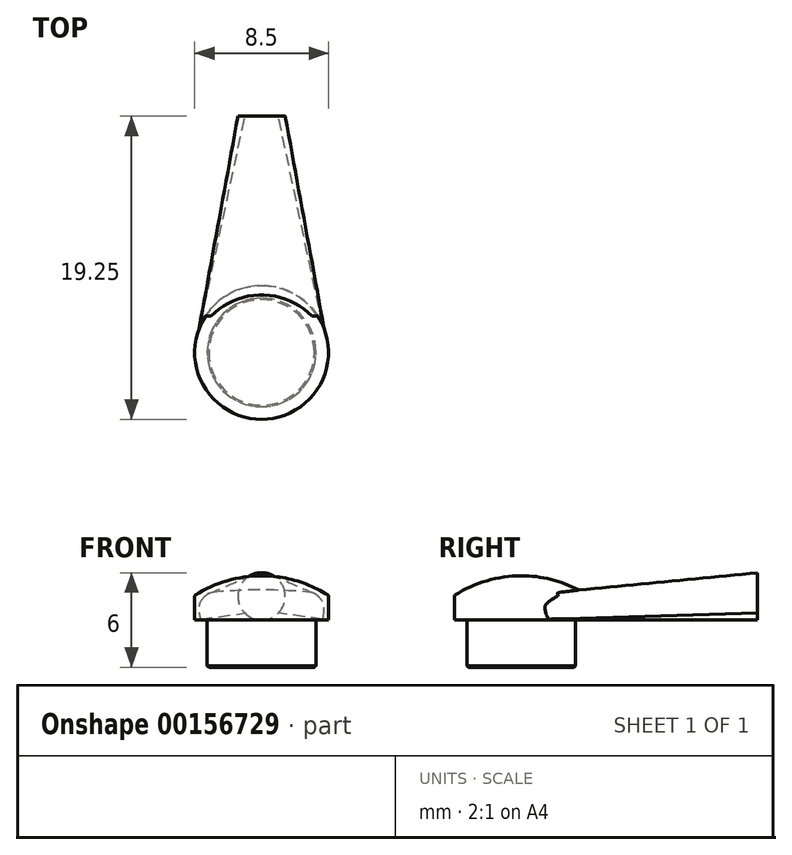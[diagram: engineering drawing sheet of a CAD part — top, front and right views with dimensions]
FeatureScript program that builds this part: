
annotation { "Feature Type Name" : "Feature", "Feature Type Description" : "" }
export const myFeature = defineFeature(function(context is Context, id is Id, definition is map)
    precondition{}
    {
        {
            var Q0;
            Q0=qCreatedBy(makeId("Top.planeOp"),FACE);
            var sketch = newSketch(context, id + "F0", { "sketchPlane" : qUnion([Q0])});
            skArc(sketch, "E0", {"start": v(-4.25, 0) * mm, "mid": v(0, -4.25) * mm, "end": v(4.25, 0) * mm});
            skArc(sketch, "E1", {"start": v(4.25, 0) * mm, "mid": v(0, 4.25) * mm, "end": v(-4.25, 0) * mm});
            skSolve(sketch);
        }
        {
            var Q0;
            Q0=makeQuery(id+"F0.imprint","IMPRINT",FACE,{"disambiguationData":[TD([[makeQuery(id+"F0.imprint","IMPRINT",EDGE,{"derivedFrom":sQuery(id+"F0.wireOp",EDGE,"E0")}),1.0]])]});
            var sketch = newSketch(context, id + "F1", { "sketchPlane" : qUnion([Q0])});
            skCircle(sketch, "E2", {"center": v(0, 0) * mm, "radius": 3.45 * mm});
            skSolve(sketch);
        }
        {
            var Q0;
            Q0=makeQuery(id+"F1.imprint","IMPRINT",FACE,{"disambiguationData":[TD([[makeQuery(id+"F1.imprint","IMPRINT",EDGE,{"derivedFrom":sQuery(id+"F1.wireOp",EDGE,"E2")}),1.0]])]});
            extrude(context, id + "F2", {"entities" : qUnion([Q0]), "oppositeDirection" : true, "depth" : 3 * mm});
        }
        {
            var Q0;
            Q0=makeQuery(id+"F2.opExtrude","CAP_EDGE",EDGE,{"disambiguationData":[OSD([sQuery(id+"F1.wireOp",EDGE,"E2")])],"isStart":false});
            chamfer(context, id + "F3", {"entities" : qUnion([Q0]), "width" : .1 * mm, "tangentPropagation" : true});
        }
        {
            var Q0;
            Q0=qCreatedBy(makeId("Front.planeOp"),FACE);
            var sketch = newSketch(context, id + "F4", { "sketchPlane" : qUnion([Q0])});
            skLineSegment(sketch, "E3.0", {"start": v(0, 0) * mm, "end": v(4.25, 0) * mm, "construction": true});
            skLineSegment(sketch, "E4.bottom", {"start": v(0, 0) * mm, "end": v(4.25, 0) * mm});
            skLineSegment(sketch, "E4.right", {"start": v(4.25, 0) * mm, "end": v(4.25, 1.55) * mm});
            skPoint(sketch, "E5.visualSharp", {"position": v(-3.75, 1.25) * mm});
            skPoint(sketch, "E6.visualSharp", {"position": v(4.25, 1.25) * mm});
            skPoint(sketch, "E7.orphan", {"position": v(-3.5, 1.25) * mm});
            skPoint(sketch, "E8.orphan", {"position": v(-4.25, 0) * mm});
            skPoint(sketch, "E9.orphan", {"position": v(3.5, 1.25) * mm});
            skPoint(sketch, "E10.end.orphan", {"position": v(0, 2.81) * mm});
            skPoint(sketch, "E11.end.orphan", {"position": v(0, 1.25) * mm});
            skArc(sketch, "E12", {"start": v(4.25, 1.55) * mm, "mid": v(2.22, 2.49) * mm, "end": v(0, 2.81) * mm});
            skLineSegment(sketch, "E13", {"start": v(0, 2.81) * mm, "end": v(0, 0) * mm});
            skSolve(sketch);
        }
        {
            var Q0;
            Q0 = qSketchRegion(id + "F4", true);
            var Q1;
            Q1=sQuery(id+"F4.wireOp",EDGE,"E13");
            revolve(context, id + "F5", {"operationType" : NewBodyOperationType.ADD, "entities" : qUnion([Q0]), "axis" : qUnion([Q1]), "revolveType" : RevolveType.FULL});
        }
        {
            var Q0;
            Q0=qCreatedBy(makeId("Front.planeOp"),FACE);
            var sketch = newSketch(context, id + "F6", { "sketchPlane" : qUnion([Q0])});
            skLineSegment(sketch, "E14.0", {"start": v(-4.25, 0.8) * mm, "end": v(4.25, 0.8) * mm, "construction": true});
            skLineSegment(sketch, "E14.1", {"start": v(-4.25, 0) * mm, "end": v(4.25, 0) * mm, "construction": true});
            skLineSegment(sketch, "E15.bottom", {"start": v(-4.25, 0) * mm, "end": v(4.25, 0) * mm});
            skLineSegment(sketch, "E15.top", {"start": v(-3.5, 1.55) * mm, "end": v(3.5, 1.55) * mm});
            skLineSegment(sketch, "E15.left", {"start": v(-4.25, 0) * mm, "end": v(-4.25, 0.8) * mm});
            skLineSegment(sketch, "E15.right", {"start": v(4.25, 0) * mm, "end": v(4.25, 0.8) * mm});
            skPoint(sketch, "E16.visualSharp", {"position": v(-4.25, 1.55) * mm});
            skArc(sketch, "E16.filletArc", {"start": v(-3.5, 1.55) * mm, "mid": v(-4.03, 1.33) * mm, "end": v(-4.25, 0.8) * mm});
            skPoint(sketch, "E17.visualSharp", {"position": v(4.25, 1.55) * mm});
            skArc(sketch, "E17.filletArc", {"start": v(4.25, 0.8) * mm, "mid": v(4.03, 1.33) * mm, "end": v(3.5, 1.55) * mm});
            skLineSegment(sketch, "E18", {"start": v(2.97, 1.33) * mm, "end": v(3.5, 0.8) * mm, "construction": true});
            skLineSegment(sketch, "E19", {"start": v(-4.25, 0.8) * mm, "end": v(3.5, 0.8) * mm, "construction": true});
            skLineSegment(sketch, "E20", {"start": v(-2.97, 1.33) * mm, "end": v(-3.5, 0.8) * mm, "construction": true});
            skLineSegment(sketch, "E21", {"start": v(-3.5, 0.8) * mm, "end": v(4.25, 0.8) * mm, "construction": true});
            skSolve(sketch);
        }
        {
            var Q0;
            Q0=qCreatedBy(makeId("Front.planeOp"),FACE);
            cPlane(context, id + "F7", {"entities" : qUnion([Q0]), "cplaneType" : CPlaneType.OFFSET, "offset" : 15 * mm, "oppositeDirection" : true, "width" : 150 * mm, "height" : 150 * mm});
        }
        {
            var Q0;
            Q0=qCreatedBy(id+"F7.planeOp",FACE);
            var sketch = newSketch(context, id + "F8", { "sketchPlane" : qUnion([Q0])});
            skPoint(sketch, "E22", {"position": v(1.38, 1.25) * mm});
            skPoint(sketch, "E23", {"position": v(1.62, 1.5) * mm});
            skPoint(sketch, "E24", {"position": v(-1.62, 0.62) * mm});
            skPoint(sketch, "E25", {"position": v(-1.38, 1.25) * mm});
            skPoint(sketch, "E26.end.orphan", {"position": v(1.62, 3) * mm});
            skPoint(sketch, "E27.orphan", {"position": v(1.62, 0) * mm});
            skPoint(sketch, "E28.end.orphan", {"position": v(-1.62, 1.25) * mm});
            skPoint(sketch, "E29.bottom.end.orphan", {"position": v(-1.62, 0) * mm});
            skArc(sketch, "E30", {"start": v(1.06, 0.44) * mm, "mid": v(0, 3) * mm, "end": v(-1.06, 0.44) * mm});
            skArc(sketch, "E31", {"start": v(-1.06, 0.44) * mm, "mid": v(0, 0) * mm, "end": v(1.06, 0.44) * mm});
            skLineSegment(sketch, "E32", {"start": v(0, 1.5) * mm, "end": v(1.62, 1.5) * mm, "construction": true});
            skLineSegment(sketch, "E33", {"start": v(1.06, 0.44) * mm, "end": v(0, 1.5) * mm, "construction": true});
            skLineSegment(sketch, "E34", {"start": v(0, 1.5) * mm, "end": v(-1.06, 0.44) * mm, "construction": true});
            skLineSegment(sketch, "E35.0", {"start": v(4.25, 0) * mm, "end": v(-4.25, 0) * mm, "construction": true});
            skSolve(sketch);
        }
        {
            var Q1;
            Q1 = qSketchRegion(id + "F6", true);
            var Q2;
            Q2 = qSketchRegion(id + "F8", true);
            var Q3;
            Q3=sQuery(id+"F8.wireOp",VERTEX,"E29.bottom.start");
            var Q4;
            Q4=sQuery(id+"F6.wireOp",VERTEX,"E15.bottom.end");
            loft(context, id + "F9", {"operationType" : NewBodyOperationType.ADD, "sheetProfilesArray" : [{ "sheetProfileEntities" : qUnion([Q1]) }, { "sheetProfileEntities" : qUnion([Q2]) }], "connections" : [{ "connectionEntities" : qUnion([Q3, Q4]), "connectionEdgeQueries" : qUnion([]), "connectionEdgeParameters" : [] }]});
        }
        {
            var Q0;
            Q0=makeQuery(id+"F9.boolean.opBoolean","SPLIT",EDGE,{"disambiguationData":[OD(0.0)],"derivedFrom":makeQuery(id+"F5.opRevolve","SWEPT_EDGE",EDGE,{"disambiguationData":[OSD([sQuery(id+"F4.wireOp",EDGE,"E4.right"),sQuery(id+"F4.wireOp",EDGE,"E12")])]})});
            fillet(context, id + "F10", {"entities" : qUnion([Q0]), "radius" : .1 * mm, "tangentPropagation" : true, "allowEdgeOverflow" : false});
        }
    });
